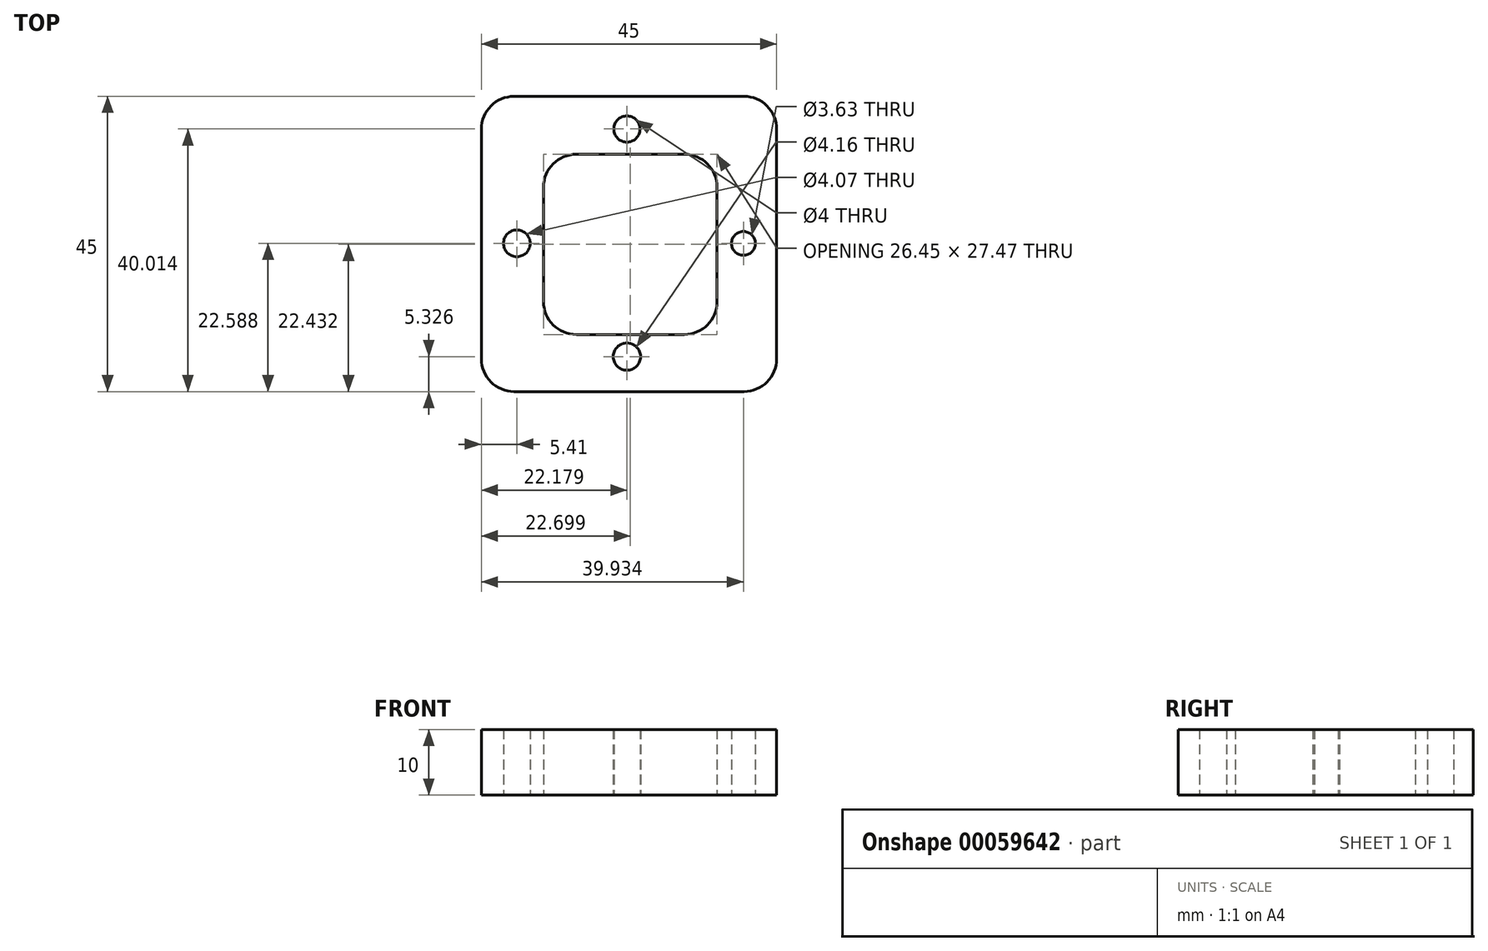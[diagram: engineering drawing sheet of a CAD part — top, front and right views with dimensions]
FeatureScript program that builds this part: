
annotation { "Feature Type Name" : "Feature", "Feature Type Description" : "" }
export const myFeature = defineFeature(function(context is Context, id is Id, definition is map)
    precondition{}
    {
        {
            var Q0;
            Q0=qCreatedBy(makeId("Top.planeOp"),FACE);
            var sketch = newSketch(context, id + "F0", { "sketchPlane" : qUnion([Q0])});
            skLineSegment(sketch, "E0.bottom", {"start": v(-51.65, 53.99) * mm, "end": v(-6.65, 53.99) * mm});
            skLineSegment(sketch, "E0.top", {"start": v(-51.65, 8.99) * mm, "end": v(-6.65, 8.99) * mm});
            skLineSegment(sketch, "E0.left", {"start": v(-51.65, 53.99) * mm, "end": v(-51.65, 8.99) * mm});
            skLineSegment(sketch, "E0.right", {"start": v(-6.65, 53.99) * mm, "end": v(-6.65, 8.99) * mm});
            skLineSegment(sketch, "E1", {"start": v(-51.65, 53.99) * mm, "end": v(-40.9, 42.27) * mm});
            skLineSegment(sketch, "E2", {"start": v(-6.65, 53.99) * mm, "end": v(-17.4, 42.27) * mm});
            skLineSegment(sketch, "E3", {"start": v(-51.65, 8.99) * mm, "end": v(-40.47, 20.3) * mm});
            skLineSegment(sketch, "E4", {"start": v(-6.65, 8.99) * mm, "end": v(-17.69, 20.43) * mm});
            skLineSegment(sketch, "E5.left", {"start": v(-40.9, 42.27) * mm, "end": v(-40.9, 42.27) * mm});
            skLineSegment(sketch, "E5.right", {"start": v(-17.4, 42.27) * mm, "end": v(-17.4, 42.27) * mm});
            skLineSegment(sketch, "E6.bottom", {"start": v(-40.9, 42.27) * mm, "end": v(-17.69, 42.27) * mm});
            skLineSegment(sketch, "E6.top", {"start": v(-40.9, 20.43) * mm, "end": v(-17.69, 20.43) * mm});
            skLineSegment(sketch, "E6.left", {"start": v(-40.9, 42.27) * mm, "end": v(-40.9, 20.43) * mm});
            skLineSegment(sketch, "E6.right", {"start": v(-17.69, 42.27) * mm, "end": v(-17.69, 20.43) * mm});
            skSolve(sketch);
        }
        {
            var Q0;
            Q0=makeQuery(id+"F0.imprint","IMPRINT",FACE,{"disambiguationData":[TD([[makeQuery(id+"F0.imprint","IMPRINT",EDGE,{"derivedFrom":sQuery(id+"F0.wireOp",EDGE,"E0.bottom")}),-1.0]])]});
            var Q1;
            Q1=makeQuery(id+"F0.imprint","IMPRINT",FACE,{"disambiguationData":[TD([[makeQuery(id+"F0.imprint","IMPRINT",EDGE,{"derivedFrom":sQuery(id+"F0.wireOp",EDGE,"E0.top")}),1.0]])]});
            var Q2;
            Q2=makeQuery(id+"F0.imprint","IMPRINT",FACE,{"disambiguationData":[TD([[makeQuery(id+"F0.imprint","IMPRINT",EDGE,{"derivedFrom":sQuery(id+"F0.wireOp",EDGE,"E6.bottom")}),-1.0]])]});
            extrude(context, id + "F1", {"entities" : qUnion([Q0, Q1, Q2]), "depth" : 10 * mm});
        }
        {
            var Q0;
            Q0=qCreatedBy(makeId("Top.planeOp"),FACE);
            var sketch = newSketch(context, id + "F2", { "sketchPlane" : qUnion([Q0])});
            skLineSegment(sketch, "E7.bottom", {"start": v(-42.17, 17.69) * mm, "end": v(-15.73, 17.69) * mm});
            skLineSegment(sketch, "E7.top", {"start": v(-42.17, 45.16) * mm, "end": v(-15.73, 45.16) * mm});
            skLineSegment(sketch, "E7.left", {"start": v(-42.17, 17.69) * mm, "end": v(-42.17, 45.16) * mm});
            skLineSegment(sketch, "E7.right", {"start": v(-15.73, 17.69) * mm, "end": v(-15.73, 45.16) * mm});
            skSolve(sketch);
        }
        {
            var Q0;
            Q0 = qSketchRegion(id + "F2", true);
            extrude(context, id + "F3", {"entities" : qUnion([Q0]), "operationType" : NewBodyOperationType.REMOVE, "depth" : 25 * mm});
        }
        {
            var Q0;
            Q0=makeQuery(id+"F1.opExtrude","SWEPT_EDGE",EDGE,{"disambiguationData":[OSD([sQuery(id+"F0.wireOp",EDGE,"E0.top"),sQuery(id+"F0.wireOp",EDGE,"E0.left")])]});
            var Q1;
            Q1=makeQuery(id+"F1.opExtrude","SWEPT_EDGE",EDGE,{"disambiguationData":[OSD([sQuery(id+"F0.wireOp",EDGE,"E0.bottom"),sQuery(id+"F0.wireOp",EDGE,"E0.left"),sQuery(id+"F0.wireOp",EDGE,"E1")])]});
            var Q2;
            Q2=makeQuery(id+"F1.opExtrude","SWEPT_EDGE",EDGE,{"disambiguationData":[OSD([sQuery(id+"F0.wireOp",EDGE,"E0.bottom"),sQuery(id+"F0.wireOp",EDGE,"E0.right")])]});
            var Q3;
            Q3=makeQuery(id+"F1.opExtrude","SWEPT_EDGE",EDGE,{"disambiguationData":[OSD([sQuery(id+"F0.wireOp",EDGE,"E0.top"),sQuery(id+"F0.wireOp",EDGE,"E0.right"),sQuery(id+"F0.wireOp",EDGE,"E4")])]});
            fillet(context, id + "F4", {"entities" : qUnion([Q0, Q1, Q2, Q3]), "radius" : 5 * mm, "tangentPropagation" : true, "allowEdgeOverflow" : false});
        }
        {
            var Q0;
            Q0=makeQuery(id+"F3.boolean.opBoolean","COPY",EDGE,{"derivedFrom":makeQuery(id+"F3.opExtrude","SWEPT_EDGE",EDGE,{"disambiguationData":[OSD([sQuery(id+"F2.wireOp",EDGE,"E7.bottom"),sQuery(id+"F2.wireOp",EDGE,"E7.left")])]})});
            var Q1;
            Q1=makeQuery(id+"F3.boolean.opBoolean","COPY",EDGE,{"derivedFrom":makeQuery(id+"F3.opExtrude","SWEPT_EDGE",EDGE,{"disambiguationData":[OSD([sQuery(id+"F2.wireOp",EDGE,"E7.top"),sQuery(id+"F2.wireOp",EDGE,"E7.left")])]})});
            var Q2;
            Q2=makeQuery(id+"F3.boolean.opBoolean","COPY",EDGE,{"derivedFrom":makeQuery(id+"F3.opExtrude","SWEPT_EDGE",EDGE,{"disambiguationData":[OSD([sQuery(id+"F2.wireOp",EDGE,"E7.top"),sQuery(id+"F2.wireOp",EDGE,"E7.right")])]})});
            var Q3;
            Q3=makeQuery(id+"F3.boolean.opBoolean","COPY",EDGE,{"derivedFrom":makeQuery(id+"F3.opExtrude","SWEPT_EDGE",EDGE,{"disambiguationData":[OSD([sQuery(id+"F2.wireOp",EDGE,"E7.bottom"),sQuery(id+"F2.wireOp",EDGE,"E7.right")])]})});
            fillet(context, id + "F5", {"entities" : qUnion([Q0, Q1, Q2, Q3]), "radius" : 5 * mm, "tangentPropagation" : true, "allowEdgeOverflow" : false});
        }
        {
            var Q0;
            Q0=qCreatedBy(makeId("Top.planeOp"),FACE);
            var sketch = newSketch(context, id + "F6", { "sketchPlane" : qUnion([Q0])});
            skCircle(sketch, "E8", {"center": v(-29.47, 49) * mm, "radius": 2 * mm});
            skCircle(sketch, "E9", {"center": v(-46.24, 31.58) * mm, "radius": 2.03 * mm});
            skCircle(sketch, "E10", {"center": v(-29.47, 14.32) * mm, "radius": 2.08 * mm});
            skCircle(sketch, "E11", {"center": v(-11.72, 31.58) * mm, "radius": 1.82 * mm});
            skSolve(sketch);
        }
        {
            var Q0;
            Q0 = qSketchRegion(id + "F6", true);
            extrude(context, id + "F7", {"entities" : qUnion([Q0]), "operationType" : NewBodyOperationType.REMOVE, "depth" : 25 * mm});
        }
    });
